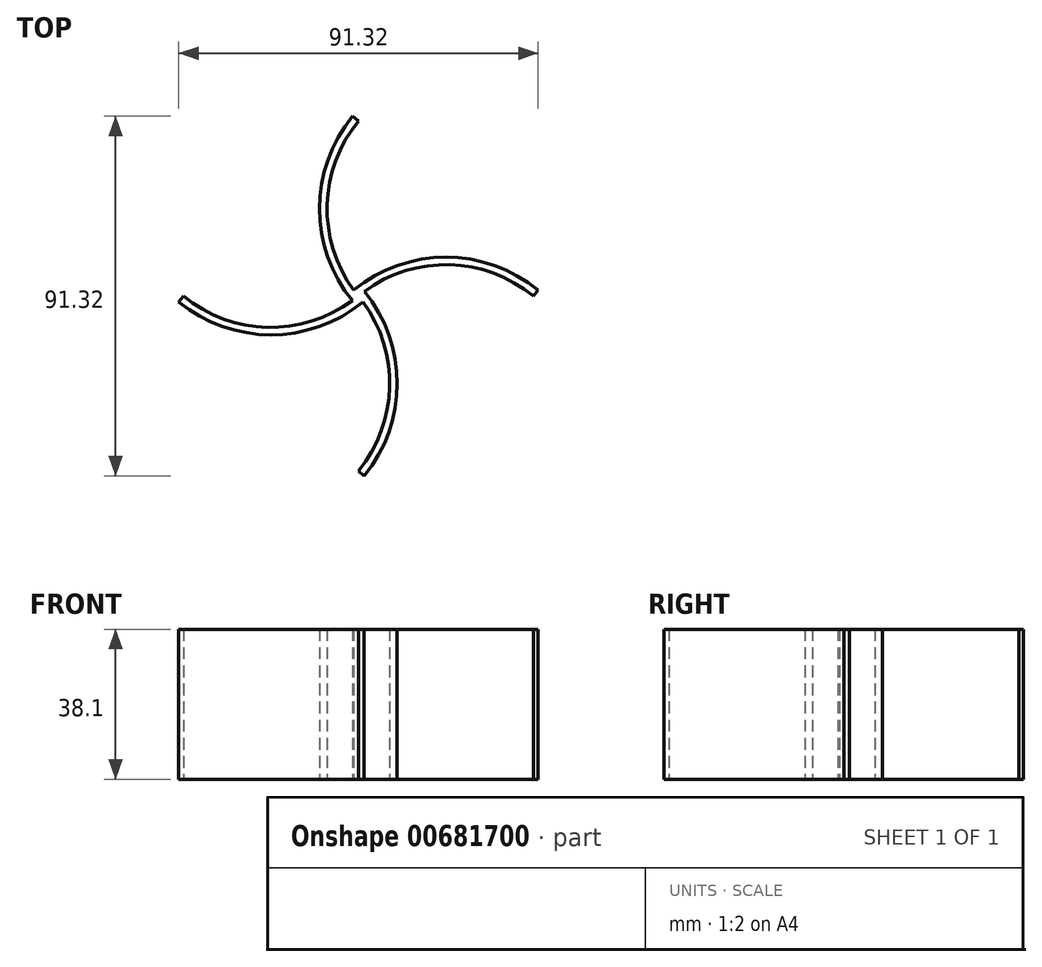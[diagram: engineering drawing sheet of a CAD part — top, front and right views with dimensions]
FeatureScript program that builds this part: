
annotation { "Feature Type Name" : "Feature", "Feature Type Description" : "" }
export const myFeature = defineFeature(function(context is Context, id is Id, definition is map)
    precondition{}
    {
        {
            var Q0;
            Q0=qCreatedBy(makeId("Top.planeOp"),FACE);
            var sketch = newSketch(context, id + "F0", { "sketchPlane" : qUnion([Q0])});
            skArc(sketch, "E0", {"start": v(0, -88.9) * mm, "mid": v(15.89, -46.36) * mm, "end": v(2.34, -3) * mm});
            skArc(sketch, "E1.0", {"start": v(2.94, -91.32) * mm, "mid": v(19.73, -44.45) * mm, "end": v(2.94, 2.42) * mm});
            skLineSegment(sketch, "E2", {"start": v(0, -88.9) * mm, "end": v(2.94, -91.32) * mm});
            skArc(sketch, "E3.1.0", {"start": v(88.9, 0) * mm, "mid": v(46.36, 15.89) * mm, "end": v(3, 2.34) * mm});
            skArc(sketch, "E3.1.1", {"start": v(91.32, 2.94) * mm, "mid": v(44.45, 19.73) * mm, "end": v(-2.42, 2.94) * mm});
            skLineSegment(sketch, "E3.1.2", {"start": v(88.9, 0) * mm, "end": v(91.32, 2.94) * mm});
            skArc(sketch, "E3.2.0", {"start": v(0, 88.9) * mm, "mid": v(-15.89, 46.36) * mm, "end": v(-2.34, 3) * mm});
            skArc(sketch, "E3.2.1", {"start": v(-2.94, 91.32) * mm, "mid": v(-19.73, 44.45) * mm, "end": v(-2.94, -2.42) * mm});
            skLineSegment(sketch, "E3.2.2", {"start": v(0, 88.9) * mm, "end": v(-2.94, 91.32) * mm});
            skArc(sketch, "E3.3.0", {"start": v(-88.9, 0) * mm, "mid": v(-46.36, -15.89) * mm, "end": v(-3, -2.34) * mm});
            skArc(sketch, "E3.3.1", {"start": v(-91.32, -2.94) * mm, "mid": v(-44.45, -19.73) * mm, "end": v(2.42, -2.94) * mm});
            skLineSegment(sketch, "E3.3.2", {"start": v(-88.9, 0) * mm, "end": v(-91.32, -2.94) * mm});
            skPoint(sketch, "E3.center", {"position": v(0, 0) * mm});
            skSolve(sketch);
        }
        {
            var Q0;
            Q0 = qSketchRegion(id + "F0", true);
            extrude(context, id + "F1", {"entities" : qUnion([Q0]), "depth" : 76.2 * mm, "offsetDistance" : 25.4 * mm});
        }
        {
            var Q0;
            Q0=makeQuery(id+"F1.opExtrude","SWEPT_BODY",BODY,{"disambiguationData":[OSD([sQuery(id+"F0.wireOp",EDGE,"E0"),sQuery(id+"F0.wireOp",EDGE,"E1.0"),sQuery(id+"F0.wireOp",EDGE,"E2"),sQuery(id+"F0.wireOp",EDGE,"E3.1.0"),sQuery(id+"F0.wireOp",EDGE,"E3.1.1"),sQuery(id+"F0.wireOp",EDGE,"E3.1.2"),sQuery(id+"F0.wireOp",EDGE,"E3.2.0"),sQuery(id+"F0.wireOp",EDGE,"E3.2.1"),sQuery(id+"F0.wireOp",EDGE,"E3.2.2"),sQuery(id+"F0.wireOp",EDGE,"E3.3.0"),sQuery(id+"F0.wireOp",EDGE,"E3.3.1"),sQuery(id+"F0.wireOp",EDGE,"E3.3.2")])]});
            var Q1;
            Q1=qCreatedBy(makeId("Origin.pointOp"),VERTEX);
            transform(context, id + "F2", {"entities" : qUnion([Q0]), "transformType" : TransformType.SCALE_UNIFORMLY, "scale" : .5, "scalePoint" : qUnion([Q1]), "makeCopy" : false});
        }
    });
